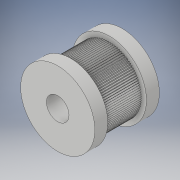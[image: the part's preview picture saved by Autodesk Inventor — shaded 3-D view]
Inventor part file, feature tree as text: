
AUTODESK INVENTOR PART (.ipt)
format: ipt  version: 2019 (Build 230136000, 136)  size: 550,912 bytes
history: native  units: mm
features: extrude x5, sketch x5, pattern_circular x1, plane x1, mirror x1
ambient origin geometry x8: Origin, YZ Plane, XZ Plane, XY Plane, X Axis, Y Axis, Z Axis, Center Point
bodies: Solid1 (feature_tree)
feature tree (13):
  extrude  "Extrusion1"  Depth=20.0mm TaperAngle=0.0deg
  extrude  "Extrusion2"  TaperAngle=30.0deg  [1 undecoded]
  pattern_circular  "Circular Pattern1"  Count=2  [1 undecoded]
  extrude  "Extrusion3"  Depth=1.0mm TaperAngle=360.0deg
  plane  "Work Plane1"
  mirror  "Mirror1"
  extrude  "Extrusion4"  Depth=1.0mm
  extrude  "Extrusion5"  Depth=4.0mm TaperAngle=0.0deg
  sketch  "Sketch1"  dims[d0=20.0mm d1=20.0mm d2=0.0mm]
  sketch  "Sketch2"  dims[d3=30.0deg d9=30.0deg]
  sketch  "Sketch3"  dims[d10=30.0deg]
  sketch  "Sketch4"  dims[d11=0.5mm]
  sketch  "Sketch5"  dims[d12=0.5mm d13=20.0mm d14=0.0mm d15=1080.0mm d16=360.0deg d18=23.0mm d19=4.0mm d20=0.0mm d21=10.0mm d22=7.0mm d23=20.0mm d24=0.0mm d25=15.0mm d26=1.0mm d27=0.0mm]
note: 2 required parameter values undecoded (feature->parameter linkage not recoverable at this tier; creation-order binding heuristic only, values carry confidence <= 0.55)
